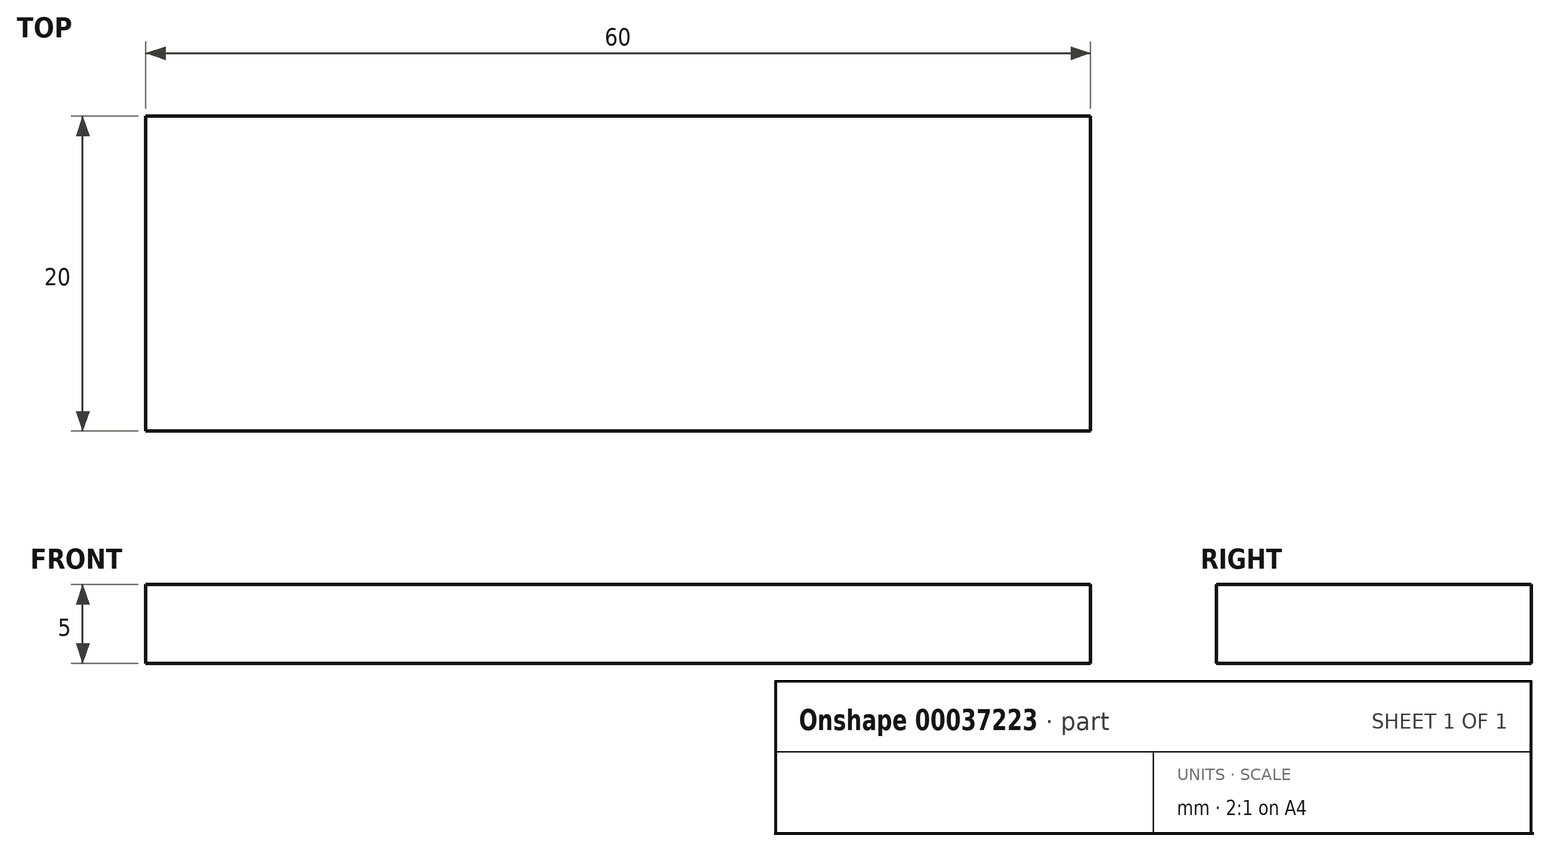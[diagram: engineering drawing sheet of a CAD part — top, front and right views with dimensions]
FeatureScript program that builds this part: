
annotation { "Feature Type Name" : "Feature", "Feature Type Description" : "" }
export const myFeature = defineFeature(function(context is Context, id is Id, definition is map)
    precondition{}
    {
        {
            var Q0;
            Q0=qCreatedBy(makeId("Top.planeOp"),FACE);
            var sketch = newSketch(context, id + "F0", { "sketchPlane" : qUnion([Q0])});
            skLineSegment(sketch, "E0.rect.bottom", {"start": v(30.01, 9.23) * mm, "end": v(-29.99, 9.23) * mm});
            skLineSegment(sketch, "E0.rect.top", {"start": v(30.01, -10.77) * mm, "end": v(-29.99, -10.77) * mm});
            skLineSegment(sketch, "E0.rect.left", {"start": v(30.01, 9.23) * mm, "end": v(30.01, -10.77) * mm});
            skLineSegment(sketch, "E0.rect.right", {"start": v(-29.99, 9.23) * mm, "end": v(-29.99, -10.77) * mm});
            skPoint(sketch, "E0.rect.middle", {"position": v(0.01, -0.77) * mm});
            skSolve(sketch);
        }
        {
            var Q0;
            Q0 = qSketchRegion(id + "F0", true);
            extrude(context, id + "F1", {"entities" : qUnion([Q0]), "depth" : 5 * mm});
        }
    });
